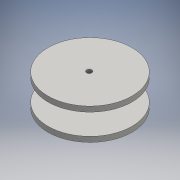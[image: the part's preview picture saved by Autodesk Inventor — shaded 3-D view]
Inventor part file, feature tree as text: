
AUTODESK INVENTOR PART (.ipt)
format: ipt  version: 2016 (Build 200138000, 138)  size: 110,080 bytes
history: native  units: mm
features: sketch x3, revolve x1, hole x1, projected_geometry x1
ambient origin geometry x8: Origin, YZ Plane, XZ Plane, XY Plane, X Axis, Y Axis, Z Axis, Center Point
bodies: Solid1 (feature_tree)
feature tree (6):
  sketch  "Sketch1"  dims[d0=50.8mm d1=6.35mm]
  revolve  "Revolution1"  [1 undecoded]
  hole  "Hole1"  [1 undecoded]
  sketch  "Sketch2"  dims[d2=12.7mm d3=25.4mm]
  sketch  "Sketch3"  dims[d4=90.0deg d5=6.35mm d6=6.35mm d7=19.05mm d8=9.525mm d9=6.35mm d10=14.3117mm d11=25.4mm d12=20.594885mm]
  projected_geometry  "Projected Loop1"
note: 2 required parameter values undecoded (feature->parameter linkage not recoverable at this tier; creation-order binding heuristic only, values carry confidence <= 0.55)